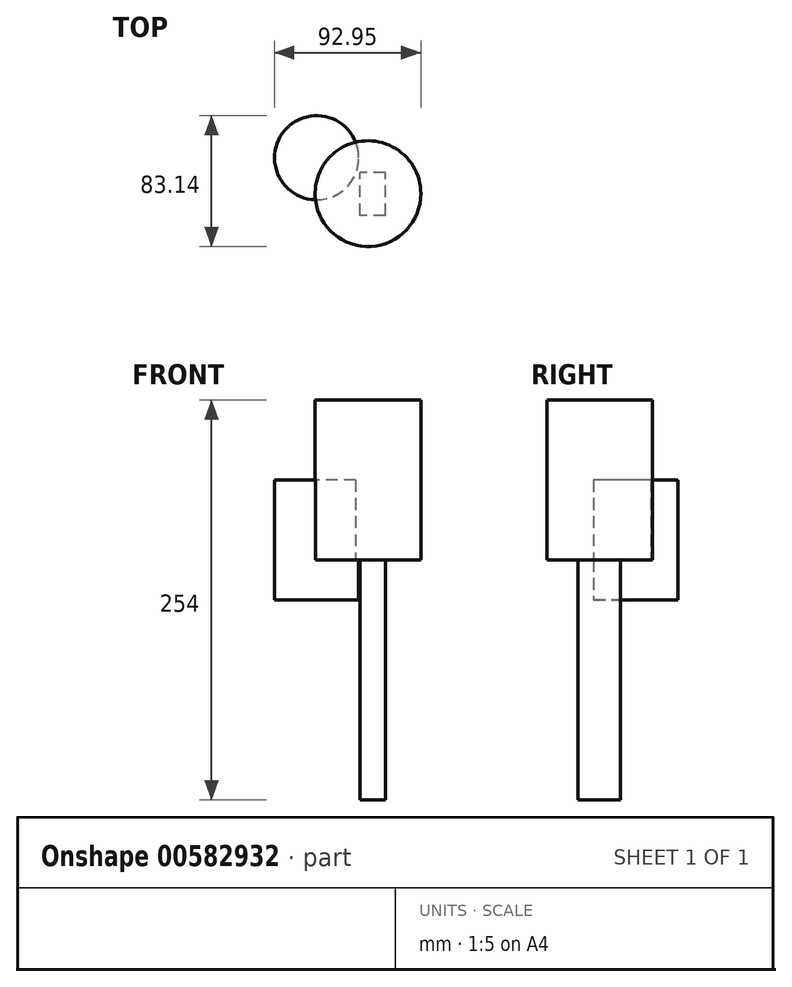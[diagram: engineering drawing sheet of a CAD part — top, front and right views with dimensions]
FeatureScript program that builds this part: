
annotation { "Feature Type Name" : "Feature", "Feature Type Description" : "" }
export const myFeature = defineFeature(function(context is Context, id is Id, definition is map)
    precondition{}
    {
        {
            var Q0;
            Q0=qCreatedBy(makeId("Top.planeOp"),FACE);
            var sketch = newSketch(context, id + "F0", { "sketchPlane" : qUnion([Q0])});
            skCircle(sketch, "E0", {"center": v(-60.45, 36.62) * mm, "radius": 26.75 * mm});
            skSolve(sketch);
        }
        {
            var Q0;
            Q0 = qSketchRegion(id + "F0", true);
            extrude(context, id + "F1", {"entities" : qUnion([Q0]), "depth" : 50.8 * mm, "offsetDistance" : 25.4 * mm});
        }
        {
            var Q0;
            Q0=qCreatedBy(makeId("Top.planeOp"),FACE);
            var sketch = newSketch(context, id + "F2", { "sketchPlane" : qUnion([Q0])});
            skCircle(sketch, "E1", {"center": v(-27.84, 13.8) * mm, "radius": 33.59 * mm});
            skSolve(sketch);
        }
        {
            var Q0;
            Q0=makeQuery(id+"F2.imprint","IMPRINT",FACE,{"disambiguationData":[TD([[makeQuery(id+"F2.imprint","IMPRINT",EDGE,{"derivedFrom":sQuery(id+"F2.wireOp",EDGE,"E1")}),1.0]])]});
            extrude(context, id + "F3", {"entities" : qUnion([Q0]), "operationType" : NewBodyOperationType.ADD, "depth" : 101.6 * mm, "offsetDistance" : 25.4 * mm});
        }
        {
            var Q0;
            Q0=makeQuery(id+"F0.imprint","IMPRINT",FACE,{"disambiguationData":[TD([[makeQuery(id+"F0.imprint","IMPRINT",EDGE,{"derivedFrom":sQuery(id+"F0.wireOp",EDGE,"E0")}),1.0]])]});
            extrude(context, id + "F4", {"entities" : qUnion([Q0]), "operationType" : NewBodyOperationType.ADD, "oppositeDirection" : true, "depth" : -50.8 * mm, "offsetDistance" : 25.4 * mm});
        }
        {
            var Q0;
            Q0 = qSketchRegion(id + "F0", true);
            extrude(context, id + "F5", {"entities" : qUnion([Q0]), "operationType" : NewBodyOperationType.ADD, "depth" : -25.4 * mm, "offsetDistance" : 25.4 * mm});
        }
        {
            var Q0;
            Q0=qCreatedBy(makeId("Top.planeOp"),FACE);
            var sketch = newSketch(context, id + "F6", { "sketchPlane" : qUnion([Q0])});
            skLineSegment(sketch, "E2.bottom", {"start": v(-16.8, 0) * mm, "end": v(-32.74, 0) * mm});
            skLineSegment(sketch, "E2.top", {"start": v(-16.8, 27.04) * mm, "end": v(-32.74, 27.04) * mm});
            skLineSegment(sketch, "E2.left", {"start": v(-16.8, 0) * mm, "end": v(-16.8, 27.04) * mm});
            skLineSegment(sketch, "E2.right", {"start": v(-32.74, 0) * mm, "end": v(-32.74, 27.04) * mm});
            skSolve(sketch);
        }
        {
            var Q0;
            Q0 = qSketchRegion(id + "F6", true);
            extrude(context, id + "F7", {"entities" : qUnion([Q0]), "operationType" : NewBodyOperationType.ADD, "oppositeDirection" : true, "depth" : 152.4 * mm, "offsetDistance" : 25.4 * mm});
        }
    });
